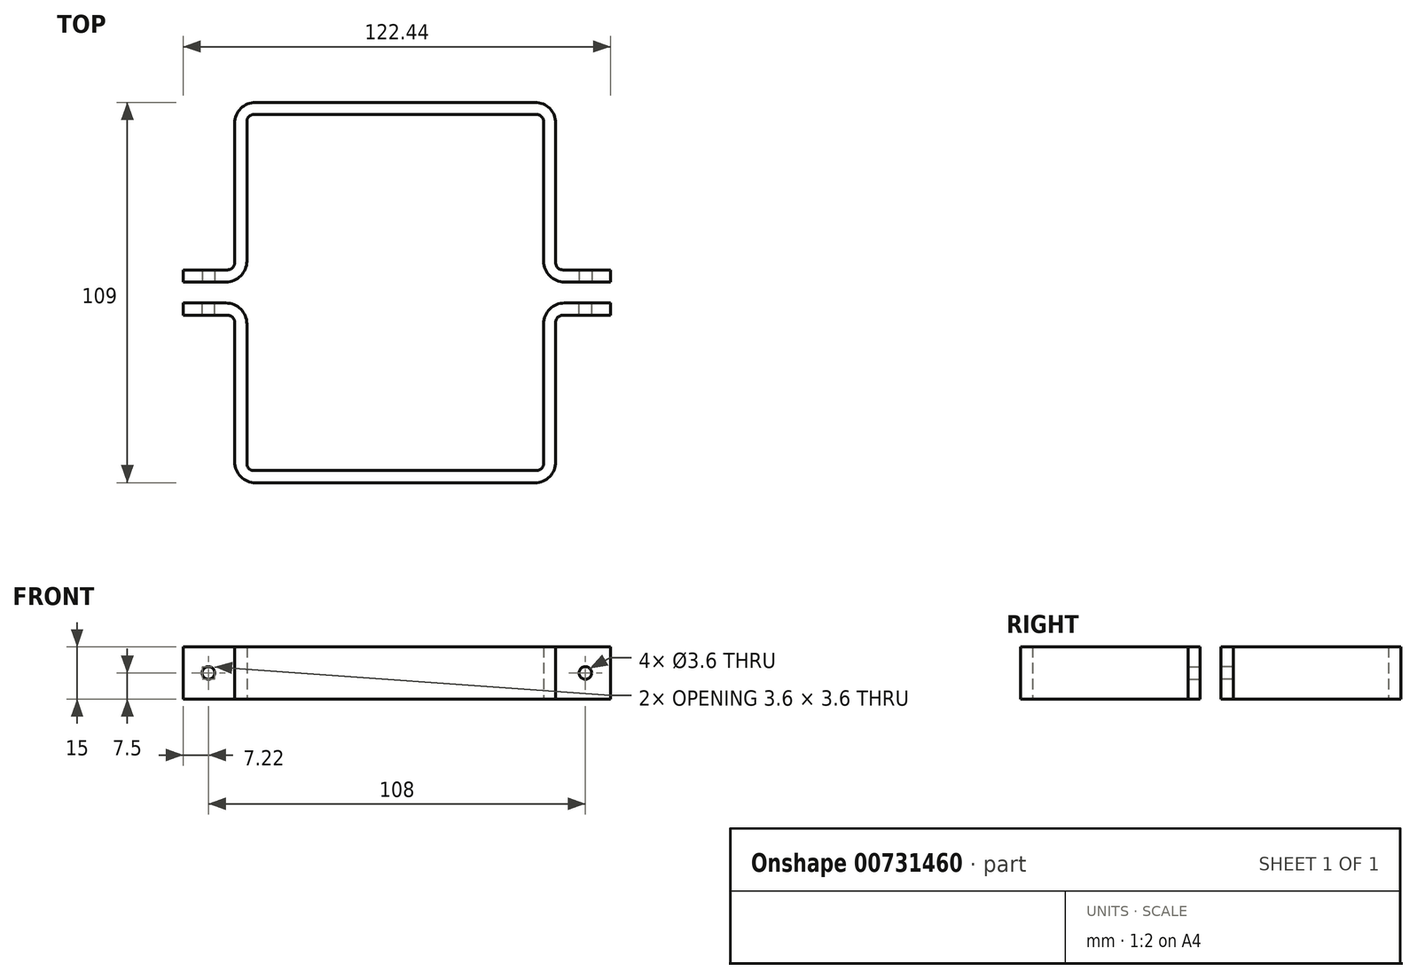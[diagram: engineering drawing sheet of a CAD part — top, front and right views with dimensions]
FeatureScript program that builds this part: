
annotation { "Feature Type Name" : "Feature", "Feature Type Description" : "" }
export const myFeature = defineFeature(function(context is Context, id is Id, definition is map)
    precondition{}
    {
        {
            var Q0;
            Q0=qCreatedBy(makeId("Top.planeOp"),FACE);
            var sketch = newSketch(context, id + "F0", { "sketchPlane" : qUnion([Q0])});
            skLineSegment(sketch, "E0.bottom", {"start": v(-61.22, 0) * mm, "end": v(-43, 0) * mm});
            skLineSegment(sketch, "E0.top", {"start": v(-61.22, 3.5) * mm, "end": v(-46.5, 3.5) * mm});
            skLineSegment(sketch, "E0.left", {"start": v(-61.22, 0) * mm, "end": v(-61.22, 3.5) * mm});
            skLineSegment(sketch, "E0.right", {"start": v(61.22, 0) * mm, "end": v(61.22, 3.5) * mm});
            skLineSegment(sketch, "E1.0", {"start": v(-43, 0) * mm, "end": v(-43, 48) * mm});
            skLineSegment(sketch, "E2.0", {"start": v(-43, 48) * mm, "end": v(42, 48) * mm});
            skLineSegment(sketch, "E3.0", {"start": v(42, 0) * mm, "end": v(42, 48) * mm});
            skLineSegment(sketch, "E4.0", {"start": v(45.5, 3.5) * mm, "end": v(45.5, 51.5) * mm});
            skLineSegment(sketch, "E4.1", {"start": v(-46.5, 51.5) * mm, "end": v(45.5, 51.5) * mm});
            skLineSegment(sketch, "E4.2", {"start": v(-46.5, 3.5) * mm, "end": v(-46.5, 51.5) * mm});
            skLineSegment(sketch, "E5.trimOffspring", {"start": v(45.5, 3.5) * mm, "end": v(61.22, 3.5) * mm});
            skLineSegment(sketch, "E6.trimOffspring", {"start": v(42, 0) * mm, "end": v(61.22, 0) * mm});
            skSolve(sketch);
        }
        {
            var Q0;
            Q0 = qSketchRegion(id + "F0", true);
            extrude(context, id + "F1", {"entities" : qUnion([Q0]), "depth" : 15 * mm, "offsetDistance" : 25 * mm, "symmetric" : true});
        }
        {
            var Q0;
            Q0=makeQuery(id+"F1.opExtrude","SWEPT_FACE",FACE,{"disambiguationData":[OSD([sQuery(id+"F0.wireOp",EDGE,"E0.top")])]});
            var sketch = newSketch(context, id + "F2", { "sketchPlane" : qUnion([Q0])});
            skPoint(sketch, "E7", {"position": v(-54, 0) * mm});
            skPoint(sketch, "E8", {"position": v(54, 0) * mm});
            skSolve(sketch);
        }
        {
            var Q0;
            Q0=sQuery(id+"F2.wireOp",VERTEX,"E8");
            var Q1;
            Q1=sQuery(id+"F2.wireOp",VERTEX,"E7");
            var Q2;
            Q2=makeQuery(id+"F1.opExtrude","SWEPT_BODY",BODY,{"disambiguationData":[OSD([sQuery(id+"F0.wireOp",EDGE,"E0.bottom"),sQuery(id+"F0.wireOp",EDGE,"E0.top"),sQuery(id+"F0.wireOp",EDGE,"E0.left"),sQuery(id+"F0.wireOp",EDGE,"E0.right"),sQuery(id+"F0.wireOp",EDGE,"E1.0"),sQuery(id+"F0.wireOp",EDGE,"E2.0"),sQuery(id+"F0.wireOp",EDGE,"E3.0"),sQuery(id+"F0.wireOp",EDGE,"E4.0"),sQuery(id+"F0.wireOp",EDGE,"E4.1"),sQuery(id+"F0.wireOp",EDGE,"E4.2"),sQuery(id+"F0.wireOp",EDGE,"E5.trimOffspring"),sQuery(id+"F0.wireOp",EDGE,"E6.trimOffspring")])]});
            hole(context, id + "F3", {"style" : HoleStyle.SIMPLE, "endStyle" : HoleEndStyle.THROUGH, "holeDiameter" : 3.6 * mm, "majorDiameter" : 5 * mm, "isTappedThrough" : true, "tappedDepth" : 12 * mm, "tapClearance" : 3, "locations" : qUnion([Q0, Q1]), "scope" : qUnion([Q2]), "startStyle" : HoleStartStyle.SKETCH});
        }
        {
            var Q0;
            Q0=makeQuery(id+"F1.opExtrude","SWEPT_EDGE",EDGE,{"disambiguationData":[OSD([sQuery(id+"F0.wireOp",EDGE,"E2.0"),sQuery(id+"F0.wireOp",EDGE,"E3.0")])]});
            var Q1;
            Q1=makeQuery(id+"F1.opExtrude","SWEPT_EDGE",EDGE,{"disambiguationData":[OSD([sQuery(id+"F0.wireOp",EDGE,"E1.0"),sQuery(id+"F0.wireOp",EDGE,"E2.0")])]});
            var Q2;
            Q2=makeQuery(id+"F1.opExtrude","SWEPT_EDGE",EDGE,{"disambiguationData":[OSD([sQuery(id+"F0.wireOp",EDGE,"E0.top"),sQuery(id+"F0.wireOp",EDGE,"E4.2")])]});
            var Q3;
            Q3=makeQuery(id+"F1.opExtrude","SWEPT_EDGE",EDGE,{"disambiguationData":[OSD([sQuery(id+"F0.wireOp",EDGE,"E4.0"),sQuery(id+"F0.wireOp",EDGE,"E5.trimOffspring")])]});
            fillet(context, id + "F4", {"entities" : qUnion([Q0, Q1, Q2, Q3]), "radius" : 2 * mm, "tangentPropagation" : true, "allowEdgeOverflow" : false});
        }
        {
            var Q0;
            Q0=makeQuery(id+"F1.opExtrude","SWEPT_EDGE",EDGE,{"disambiguationData":[OSD([sQuery(id+"F0.wireOp",EDGE,"E4.0"),sQuery(id+"F0.wireOp",EDGE,"E4.1")])]});
            var Q1;
            Q1=makeQuery(id+"F1.opExtrude","SWEPT_EDGE",EDGE,{"disambiguationData":[OSD([sQuery(id+"F0.wireOp",EDGE,"E4.1"),sQuery(id+"F0.wireOp",EDGE,"E4.2")])]});
            var Q2;
            Q2=makeQuery(id+"F1.opExtrude","SWEPT_EDGE",EDGE,{"disambiguationData":[OSD([sQuery(id+"F0.wireOp",EDGE,"E3.0"),sQuery(id+"F0.wireOp",EDGE,"E6.trimOffspring")])]});
            var Q3;
            Q3=makeQuery(id+"F1.opExtrude","SWEPT_EDGE",EDGE,{"disambiguationData":[OSD([sQuery(id+"F0.wireOp",EDGE,"E0.bottom"),sQuery(id+"F0.wireOp",EDGE,"E1.0")])]});
            fillet(context, id + "F5", {"entities" : qUnion([Q0, Q1, Q2, Q3]), "radius" : 6 * mm, "tangentPropagation" : true, "allowEdgeOverflow" : false});
        }
        {
            var Q0;
            Q0=qCreatedBy(makeId("Top.planeOp"),FACE);
            var sketch = newSketch(context, id + "F6", { "sketchPlane" : qUnion([Q0])});
            skLineSegment(sketch, "E9.0", {"start": v(-61.22, 0) * mm, "end": v(-61.22, 3.5) * mm});
            skLineSegment(sketch, "E10.0", {"start": v(61.22, 0) * mm, "end": v(61.22, 3.5) * mm});
            skLineSegment(sketch, "E11.0", {"start": v(-40.5, 51.5) * mm, "end": v(39.5, 51.5) * mm});
            skLineSegment(sketch, "E12.bottom", {"start": v(-61.22, 0) * mm, "end": v(61.22, 0) * mm});
            skLineSegment(sketch, "E12.top", {"start": v(-61.22, 51.5) * mm, "end": v(61.22, 51.5) * mm});
            skLineSegment(sketch, "E12.left", {"start": v(-61.22, 0) * mm, "end": v(-61.22, 51.5) * mm});
            skLineSegment(sketch, "E12.right", {"start": v(61.22, 0) * mm, "end": v(61.22, 51.5) * mm});
            skSolve(sketch);
        }
        {
            var Q0;
            Q0=qCreatedBy(makeId("Front.planeOp"),FACE);
            cPlane(context, id + "F7", {"entities" : qUnion([Q0]), "cplaneType" : CPlaneType.OFFSET, "offset" : 3 * mm, "width" : 150 * mm, "height" : 150 * mm});
        }
        {
            var Q0;
            Q0=makeQuery(id+"F1.opExtrude","SWEPT_BODY",BODY,{"disambiguationData":[OSD([sQuery(id+"F0.wireOp",EDGE,"E0.bottom"),sQuery(id+"F0.wireOp",EDGE,"E0.top"),sQuery(id+"F0.wireOp",EDGE,"E0.left"),sQuery(id+"F0.wireOp",EDGE,"E0.right"),sQuery(id+"F0.wireOp",EDGE,"E1.0"),sQuery(id+"F0.wireOp",EDGE,"E2.0"),sQuery(id+"F0.wireOp",EDGE,"E3.0"),sQuery(id+"F0.wireOp",EDGE,"E4.0"),sQuery(id+"F0.wireOp",EDGE,"E4.1"),sQuery(id+"F0.wireOp",EDGE,"E4.2"),sQuery(id+"F0.wireOp",EDGE,"E5.trimOffspring"),sQuery(id+"F0.wireOp",EDGE,"E6.trimOffspring")])]});
            var Q1;
            Q1=qCreatedBy(id+"F7.planeOp",FACE);
            mirror(context, id + "F8", {"entities" : qUnion([Q0]), "mirrorPlane" : qUnion([Q1])});
        }
    });
